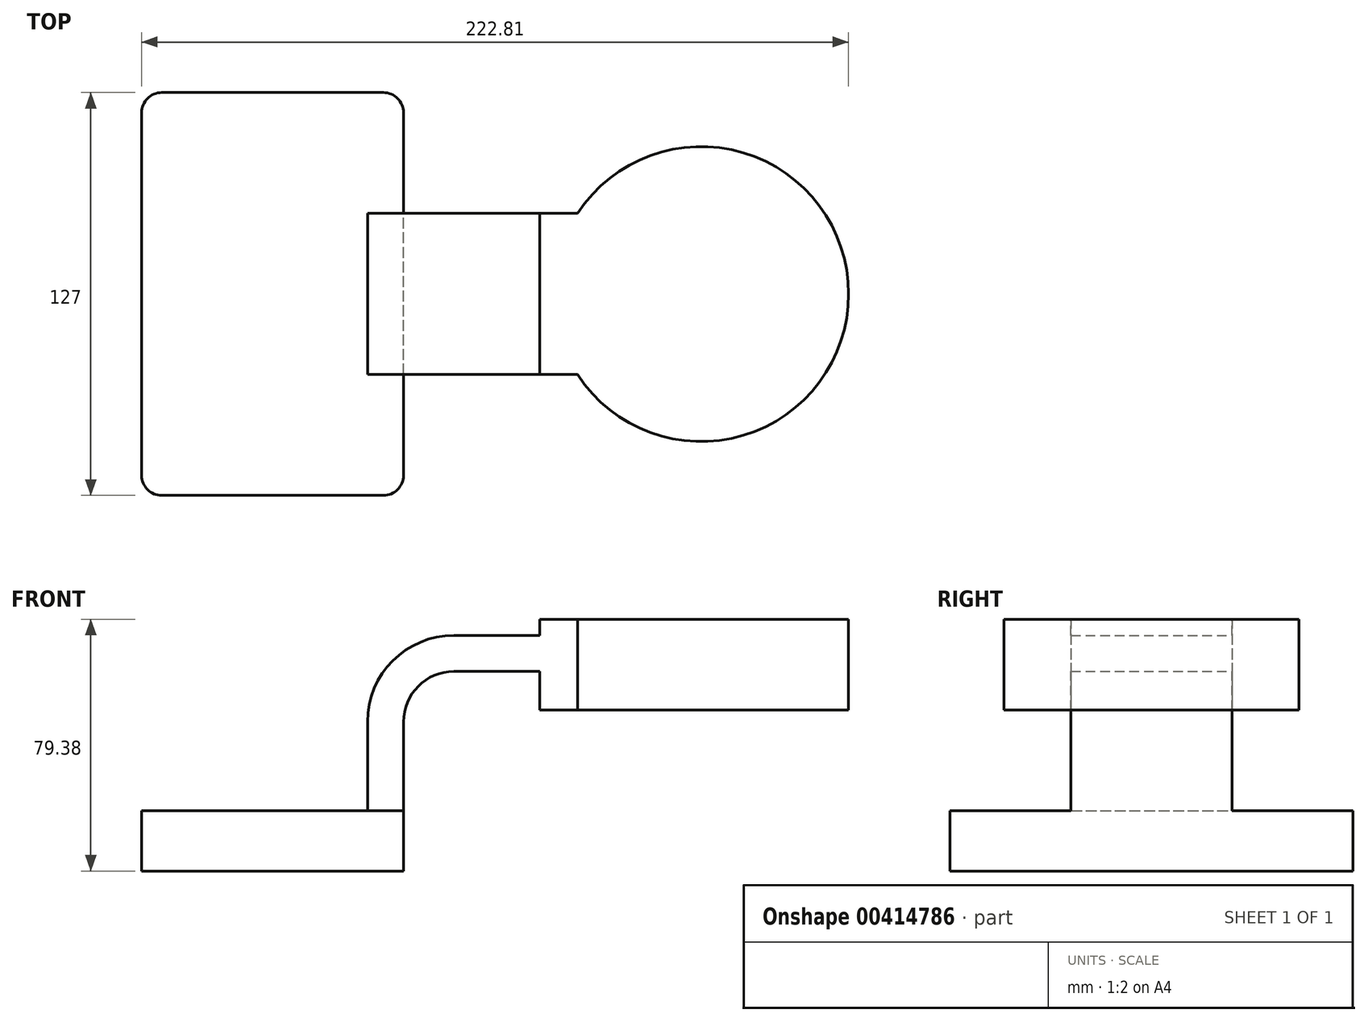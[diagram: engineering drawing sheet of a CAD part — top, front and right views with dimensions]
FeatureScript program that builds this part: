
annotation { "Feature Type Name" : "Feature", "Feature Type Description" : "" }
export const myFeature = defineFeature(function(context is Context, id is Id, definition is map)
    precondition{}
    {
        {
            var Q0;
            Q0=qCreatedBy(makeId("Front.planeOp"),FACE);
            var sketch = newSketch(context, id + "F0", { "sketchPlane" : qUnion([Q0])});
            skLineSegment(sketch, "E0.bottom", {"start": v(41.28, -9.52) * mm, "end": v(-41.28, -9.53) * mm});
            skLineSegment(sketch, "E0.top", {"start": v(41.28, 9.53) * mm, "end": v(-41.28, 9.53) * mm});
            skLineSegment(sketch, "E0.left", {"start": v(41.28, -9.52) * mm, "end": v(41.28, 9.53) * mm});
            skLineSegment(sketch, "E0.right", {"start": v(-41.28, -9.52) * mm, "end": v(-41.28, 9.53) * mm});
            skPoint(sketch, "E0.middle", {"position": v(0, 0) * mm});
            skLineSegment(sketch, "E1.bottom", {"start": v(84.26, 41.28) * mm, "end": v(135.06, 41.28) * mm});
            skLineSegment(sketch, "E1.top", {"start": v(84.26, 69.85) * mm, "end": v(135.06, 69.85) * mm});
            skLineSegment(sketch, "E1.left", {"start": v(84.26, 41.28) * mm, "end": v(84.26, 69.85) * mm});
            skLineSegment(sketch, "E1.right", {"start": v(135.06, 41.28) * mm, "end": v(135.06, 69.85) * mm});
            skPoint(sketch, "E1.middle", {"position": v(109.66, 55.56) * mm});
            skLineSegment(sketch, "E2", {"start": v(41.28, 9.53) * mm, "end": v(41.28, 37.5) * mm});
            skArc(sketch, "E3", {"start": v(41.27, 37.5) * mm, "mid": v(45.92, 48.72) * mm, "end": v(57.15, 53.37) * mm});
            skLineSegment(sketch, "E4", {"start": v(57.15, 53.37) * mm, "end": v(88.58, 53.37) * mm});
            skLineSegment(sketch, "E5.0", {"start": v(57.15, 64.73) * mm, "end": v(88.58, 64.73) * mm});
            skArc(sketch, "E5.1", {"start": v(29.9, 37.5) * mm, "mid": v(37.89, 56.75) * mm, "end": v(57.15, 64.73) * mm});
            skLineSegment(sketch, "E5.2", {"start": v(29.9, 9.53) * mm, "end": v(29.9, 37.5) * mm});
            skLineSegment(sketch, "E6", {"start": v(88.58, 41.28) * mm, "end": v(88.58, 69.85) * mm});
            skFitSpline(sketch, "E7", {"points": [v(-41.28, 9.53) * mm, v(78.4, 64.73) * mm], "startDerivative": vector(14.16, 86.96) * mm, "endDerivative": vector(328.42, -26.31) * mm});
            skSolve(sketch);
        }
        {
            var Q0;
            Q0=makeQuery(id+"F0.imprint","IMPRINT",FACE,{"disambiguationData":[TD([[makeQuery(id+"F0.imprint","IMPRINT",EDGE,{"derivedFrom":sQuery(id+"F0.wireOp",EDGE,"E0.bottom")}),-1.0]])]});
            extrude(context, id + "F1", {"entities" : qUnion([Q0]), "endBound" : BoundingType.SYMMETRIC, "depth" : 127 * mm});
        }
        {
            var Q0;
            {var subQ1=sQuery(id+"F0.wireOp",EDGE,"E2");Q0=makeQuery(id+"F0.imprint","IMPRINT",FACE,{"disambiguationData":[TD([[makeQuery(id+"F0.imprint","IMPRINT",EDGE,{"derivedFrom":subQ1}),1.0]])]});}
            var Q1;
            {var subQ0=sQuery(id+"F0.wireOp",EDGE,"E1.left");var subQ1=sQuery(id+"F0.wireOp",EDGE,"E1.bottom");var subQ2=makeQuery(id+"F0.imprint","INTERSECT",VERTEX,{"derivedFrom":[subQ1,subQ0]});Q1=makeQuery(id+"F0.imprint","IMPRINT",FACE,{"disambiguationData":[TD([[makeQuery(id+"F0.imprint","IMPRINT",EDGE,{"disambiguationData":[TD([[subQ2,-1.0]])],"derivedFrom":subQ1}),1.0]])]});}
            var Q2;
            {var subQ0=sQuery(id+"F0.wireOp",EDGE,"E4");var subQ1=sQuery(id+"F0.wireOp",EDGE,"E1.left");var subQ2=makeQuery(id+"F0.imprint","INTERSECT",VERTEX,{"derivedFrom":[subQ1,subQ0]});Q2=makeQuery(id+"F0.imprint","IMPRINT",FACE,{"disambiguationData":[TD([[makeQuery(id+"F0.imprint","IMPRINT",EDGE,{"disambiguationData":[TD([[subQ2,-1.0]])],"derivedFrom":subQ1}),-1.0]])]});}
            var Q3;
            {var subQ0=sQuery(id+"F0.wireOp",EDGE,"E1.left");var subQ1=sQuery(id+"F0.wireOp",EDGE,"E1.top");var subQ2=makeQuery(id+"F0.imprint","INTERSECT",VERTEX,{"derivedFrom":[subQ1,subQ0]});Q3=makeQuery(id+"F0.imprint","IMPRINT",FACE,{"disambiguationData":[TD([[makeQuery(id+"F0.imprint","IMPRINT",EDGE,{"disambiguationData":[TD([[subQ2,-1.0]])],"derivedFrom":subQ1}),-1.0]])]});}
            var Q4;
            {var subQ4=sQuery(id+"F0.wireOp",EDGE,"E1.right");Q4=makeQuery(id+"F0.imprint","IMPRINT",FACE,{"disambiguationData":[TD([[makeQuery(id+"F0.imprint","IMPRINT",EDGE,{"derivedFrom":subQ4}),1.0]])]});}
            extrude(context, id + "F2", {"entities" : qUnion([Q0, Q1, Q2, Q3, Q4]), "operationType" : NewBodyOperationType.ADD, "endBound" : BoundingType.SYMMETRIC, "depth" : 50.8 * mm});
        }
        {
            var Q0;
            {var subQ1=sQuery(id+"F0.wireOp",EDGE,"E5.1");Q0=makeQuery(id+"F0.imprint","IMPRINT",FACE,{"disambiguationData":[TD([[makeQuery(id+"F0.imprint","IMPRINT",EDGE,{"derivedFrom":subQ1}),1.0]])]});}
            extrude(context, id + "F3", {"entities" : qUnion([Q0]), "operationType" : NewBodyOperationType.ADD, "endBound" : BoundingType.SYMMETRIC, "depth" : 15.88 * mm});
        }
        {
            var Q0;
            {var subQ4=sQuery(id+"F0.wireOp",EDGE,"E1.right");Q0=makeQuery(id+"F0.imprint","IMPRINT",FACE,{"disambiguationData":[TD([[makeQuery(id+"F0.imprint","IMPRINT",EDGE,{"derivedFrom":subQ4}),1.0]])]});}
            var Q1;
            Q1=sQuery(id+"F0.wireOp",EDGE,"E1.right");
            revolve(context, id + "F4", {"operationType" : NewBodyOperationType.ADD, "entities" : qUnion([Q0]), "axis" : qUnion([Q1]), "revolveType" : RevolveType.FULL});
        }
        {
            var Q0;
            Q0=makeQuery(id+"F1.opExtrude","CAP_EDGE",EDGE,{"disambiguationData":[OSD([sQuery(id+"F0.wireOp",EDGE,"E0.left")])],"isStart":false});
            var Q1;
            Q1=makeQuery(id+"F1.opExtrude","CAP_EDGE",EDGE,{"disambiguationData":[OSD([sQuery(id+"F0.wireOp",EDGE,"E0.right")])],"isStart":false});
            var Q2;
            Q2=makeQuery(id+"F1.opExtrude","CAP_EDGE",EDGE,{"disambiguationData":[OSD([sQuery(id+"F0.wireOp",EDGE,"E0.left")])],"isStart":true});
            var Q3;
            Q3=makeQuery(id+"F1.opExtrude","CAP_EDGE",EDGE,{"disambiguationData":[OSD([sQuery(id+"F0.wireOp",EDGE,"E0.right")])],"isStart":true});
            fillet(context, id + "F5", {"entities" : qUnion([Q0, Q1, Q2, Q3]), "radius" : 6.35 * mm, "tangentPropagation" : true, "allowEdgeOverflow" : false});
        }
    });
